# Revit family: VOLCANO_MINI_AC
name_source: partatom
category: Mechanical Equipment
revit_build: Autodesk Revit 2017 (Build: 20170118_1100(x64)
units: mm (PartAtom-declared; Revit-internal decimal feet)

## family parameters
Cut with Voids When Loaded = No
Host = Face
Part Type = Normal
Room Calculation Point = No
Round Connector Dimension = Use Diameter
Shared = No

## types (3) — shared parameters
Connection stub pipe diameter inlet = 19 "
Connection stub pipe diameter outlet = 19 "
Default Elevation = 1219 mm
Device inlet air temperature = 0 °C
Device inlet water temperature = 70 °C
Device outlet water temperature = 50 °C
Electrical Potential = 230 V
Frequency = 50 Hz
Manufacturer = VTS
Material = <By Category>
Motor rated current AC = 1 A
Motor rated rotations [rpm] = 1450
Protection rating = IP 54
Show Range = Yes
URL = http://vtsgroup.pl
Weight = 17.50 kg

## per-type parameters (varying)
| type | AC motor power | Device heating power | Device outlet air temperature | Fan output | Heat exchanger pressure loss | Horizontal range | Medium flow | Model | Type Comments | Vertical range |
| VR MINI AC HIGH | 115 W | 15 kW | 21 °C | 2100 m³/h | 7.90 Pa | 14000 mm  [stored 45.9318 ft] | 1 m³/h | MINI AC HIGH |  | 8000 mm  [stored 26.2467 ft] |
| VR MINI AC MEDIUM | 68 W | 13 kW | 24 °C | 1650 m³/h | 6.10 Pa | 8000 mm  [stored 26.2467 ft] | 1 m³/h |  | MINI AC MEDIUM | 5000 mm  [stored 16.4042 ft] |
| VR MINI AC LOW | 48 W | 10 kW | 28 °C | 1100 m³/h | 3.90 Pa | 8000 mm  [stored 26.2467 ft] | 0 m³/h |  | MINI AC LOW | 5000 mm  [stored 16.4042 ft] |

note: [stored X ft] marks values corroborated as IEEE doubles in the binary element streams (Revit-internal decimal feet)

## geometry (parser evidence)
native form markers: Sweep x8
no freeform markers — native parametric forms only
